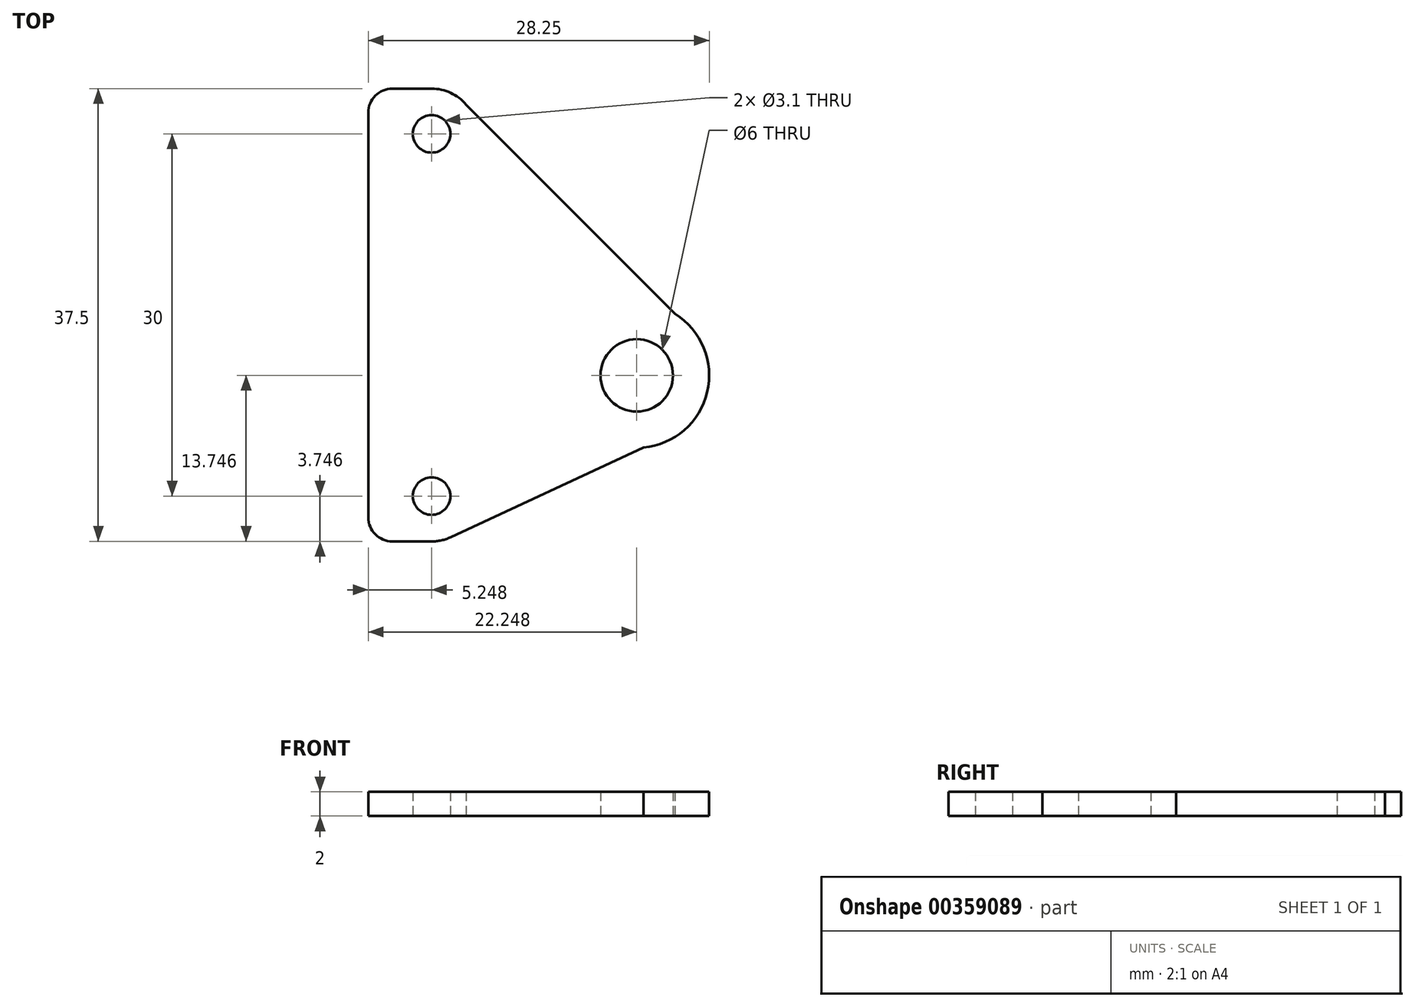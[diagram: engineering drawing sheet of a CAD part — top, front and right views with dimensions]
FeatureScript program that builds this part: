
annotation { "Feature Type Name" : "Feature", "Feature Type Description" : "" }
export const myFeature = defineFeature(function(context is Context, id is Id, definition is map)
    precondition{}
    {
        {
            var Q0;
            Q0=qCreatedBy(makeId("Top.planeOp"),FACE);
            var sketch = newSketch(context, id + "F0", { "sketchPlane" : qUnion([Q0])});
            skLineSegment(sketch, "E0", {"start": v(-16.17, 18.4) * mm, "end": v(-16.17, -11.6) * mm, "construction": true});
            skCircle(sketch, "E1", {"center": v(-16.17, 18.4) * mm, "radius": 1.55 * mm});
            skCircle(sketch, "E2", {"center": v(-16.17, -11.6) * mm, "radius": 1.55 * mm});
            skCircle(sketch, "E3", {"center": v(-16.17, 18.4) * mm, "radius": 3.75 * mm});
            skCircle(sketch, "E4", {"center": v(-16.17, -11.6) * mm, "radius": 3.75 * mm});
            skCircle(sketch, "E5", {"center": v(0.83, -1.6) * mm, "radius": 3 * mm});
            skLineSegment(sketch, "E6", {"start": v(0.83, -1.6) * mm, "end": v(-16.17, -1.6) * mm});
            skCircle(sketch, "E7", {"center": v(0.83, -1.6) * mm, "radius": 6 * mm});
            skLineSegment(sketch, "E8", {"start": v(-13.3, 20.81) * mm, "end": v(4, 3.5) * mm});
            skLineSegment(sketch, "E9", {"start": v(1.37, -7.58) * mm, "end": v(-14.6, -15) * mm});
            skLineSegment(sketch, "E10", {"start": v(-19.92, 18.4) * mm, "end": v(-19.92, -11.6) * mm, "construction": true});
            skLineSegment(sketch, "E11", {"start": v(-21.42, 3.4) * mm, "end": v(-21.42, 20.15) * mm});
            skPoint(sketch, "E11.startSnap0", {"position": v(-19.92, 3.4) * mm});
            skLineSegment(sketch, "E12", {"start": v(-21.42, 3.4) * mm, "end": v(-21.42, -13.35) * mm});
            skLineSegment(sketch, "E13", {"start": v(-16.17, 22.15) * mm, "end": v(-19.42, 22.15) * mm});
            skLineSegment(sketch, "E14", {"start": v(-16.17, -15.35) * mm, "end": v(-19.42, -15.35) * mm});
            skPoint(sketch, "E15.orphan", {"position": v(-21.42, 20.3) * mm});
            skPoint(sketch, "E16.orphan", {"position": v(-21.42, -10.1) * mm});
            skPoint(sketch, "E17.visualSharp", {"position": v(-21.42, 22.15) * mm});
            skArc(sketch, "E17.filletArc", {"start": v(-19.42, 22.15) * mm, "mid": v(-20.84, 21.56) * mm, "end": v(-21.42, 20.15) * mm});
            skPoint(sketch, "E18.visualSharp", {"position": v(-21.42, -15.35) * mm});
            skArc(sketch, "E18.filletArc", {"start": v(-21.42, -13.35) * mm, "mid": v(-20.84, -14.77) * mm, "end": v(-19.42, -15.35) * mm});
            skSolve(sketch);
        }
        {
            var Q0;
            Q0 = qSketchRegion(id + "F0", true);
            extrude(context, id + "F1", {"entities" : qUnion([Q0]), "depth" : 2 * mm, "offsetDistance" : 25 * mm});
        }
    });
